# Revit family: Рама монтажна РМ_укр
name_source: partatom
category: Mechanical Equipment
units: mm (PartAtom-declared; Revit-internal decimal feet)

## family parameters
Always vertical = Yes
Cut with Voids When Loaded = No
OmniClass Number = 23.75.00.00
OmniClass Title = Climate Control (HVAC)
Part Type = Normal
Room Calculation Point = No
Round Connector Dimension = Use Diameter
Shared = No
Work Plane-Based = No

## types (5) — shared parameters
00_20_Виробник = Вентс
00_20_Назва = Рама монтажна РМ
Матеріал зони обслуговуваня = <By Category>
Матеріал корпусу = Вуглецева сталь з порошковим покриттям
Розрахована на навантаження = 50-180  кг/м2
zero-valued in all types: Default Elevation

## per-type parameters (varying)
| type | A1 | A2 | B | C | H | L1 | L2 | L3 | c1 | h1 | Вага |
| РМ-1 | 700 mm  [stored 2.29659 ft] | 480 mm  [stored 1.5748 ft] | 865 mm  [stored 2.83793 ft] | 524 mm  [stored 1.71916 ft] | 830 mm  [stored 2.7231 ft] | 310 mm  [stored 1.01706 ft] | 449 mm  [stored 1.4731 ft] | 223 mm | 414 mm  [stored 1.35827 ft] | 827 mm  [stored 2.71325 ft] | 27.90 kg |
| РМ-2 | 700 mm  [stored 2.29659 ft] | 480 mm  [stored 1.5748 ft] | 862 mm  [stored 2.82808 ft] | 524 mm  [stored 1.71916 ft] | 807 mm | 310 mm  [stored 1.01706 ft] | 419 mm | 249 mm  [stored 0.816929 ft] | 414 mm  [stored 1.35827 ft] | 804 mm | 27.60 kg |
| РМ-3 | 820 mm  [stored 2.69029 ft] | 520 mm  [stored 1.70604 ft] | 986 mm  [stored 3.23491 ft] | 564 mm | 741 mm  [stored 2.4311 ft] | 350 mm  [stored 1.14829 ft] | 523 mm  [stored 1.71588 ft] | 269 mm | 454 mm  [stored 1.4895 ft] | 738 mm | 28.80 kg |
| РМ-4 | 700 mm  [stored 2.29659 ft] | 520 mm  [stored 1.70604 ft] | 914 mm  [stored 2.99869 ft] | 564 mm | 710 mm | 350 mm  [stored 1.14829 ft] | 418 mm  [stored 1.37139 ft] | 302 mm  [stored 0.990814 ft] | 454 mm  [stored 1.4895 ft] | 707 mm | 27.40 kg |
| РМ-5 | 700 mm  [stored 2.29659 ft] | 480 mm  [stored 1.5748 ft] | 862 mm  [stored 2.82808 ft] | 524 mm  [stored 1.71916 ft] | 800 mm  [stored 2.62467 ft] | 310 mm  [stored 1.01706 ft] | 419 mm | 249 mm  [stored 0.816929 ft] | 414 mm  [stored 1.35827 ft] | 797 mm  [stored 2.61483 ft] | 27.50 kg |

note: column(s) folded — value = type name in every type: 00_20_Тип

note: [stored X ft] marks values corroborated as IEEE doubles in the binary element streams (Revit-internal decimal feet)

## geometry (parser evidence)
native form markers: Sweep x8
no freeform markers — native parametric forms only
